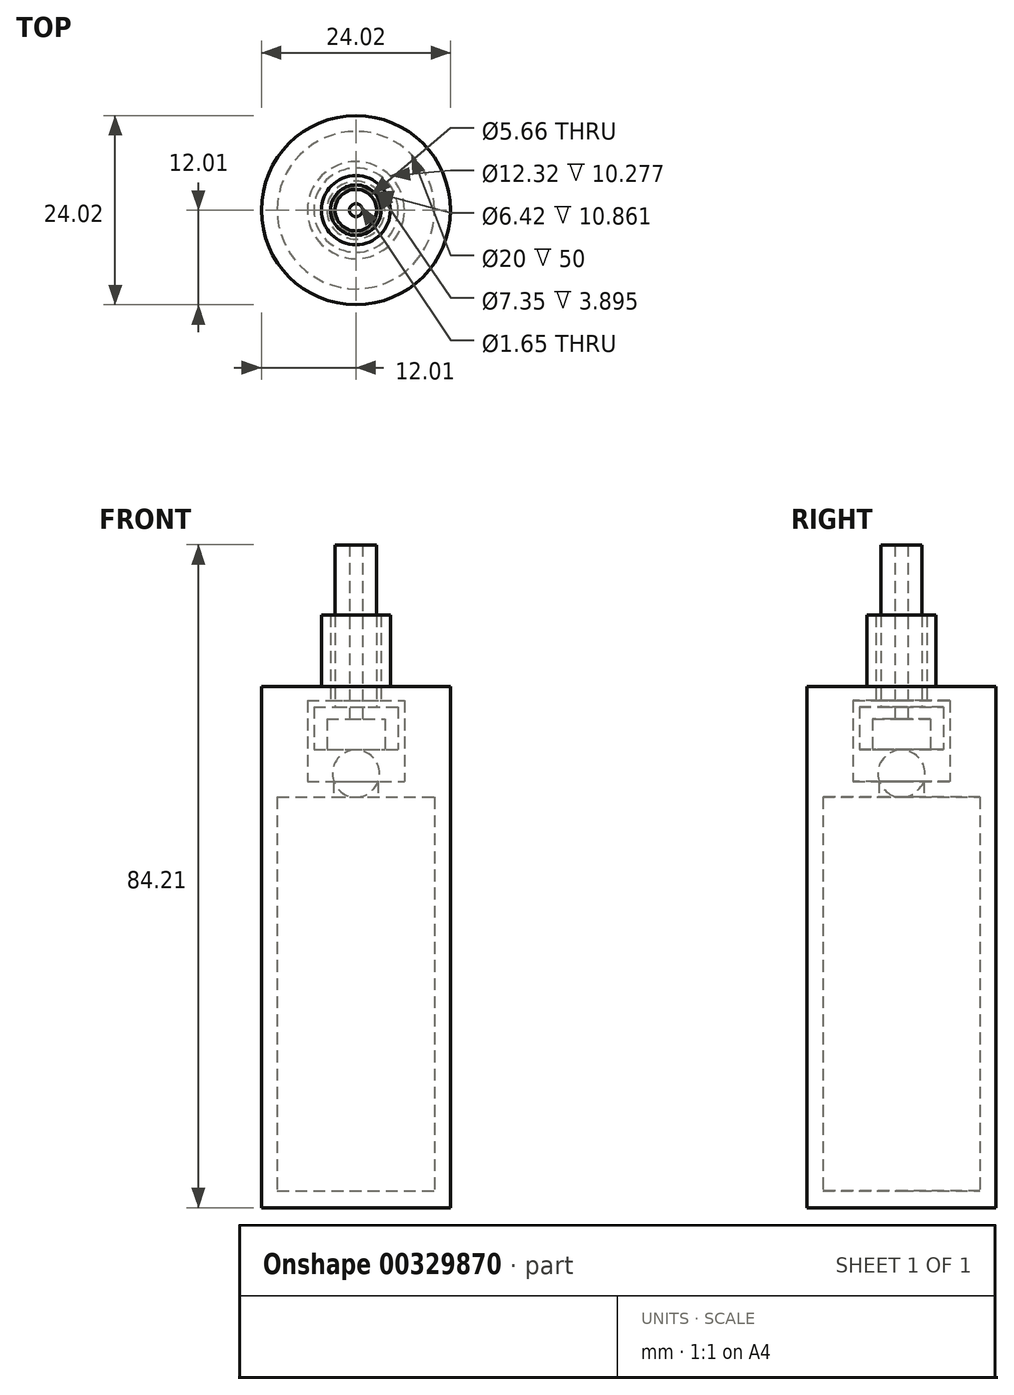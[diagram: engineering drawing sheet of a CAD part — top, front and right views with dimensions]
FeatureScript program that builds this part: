
annotation { "Feature Type Name" : "Feature", "Feature Type Description" : "" }
export const myFeature = defineFeature(function(context is Context, id is Id, definition is map)
    precondition{}
    {
        {
            var Q0;
            Q0=qCreatedBy(makeId("Front.planeOp"),FACE);
            var sketch = newSketch(context, id + "F0", { "sketchPlane" : qUnion([Q0])});
            skLineSegment(sketch, "E0", {"start": v(0, 0) * mm, "end": v(0, 40.48) * mm, "construction": true});
            skLineSegment(sketch, "E1", {"start": v(-10, 50) * mm, "end": v(-10, 0) * mm});
            skLineSegment(sketch, "E2", {"start": v(-10, 0) * mm, "end": v(0, 0) * mm});
            skLineSegment(sketch, "E3", {"start": v(-10, 50) * mm, "end": v(-2.83, 50) * mm});
            skLineSegment(sketch, "E4", {"start": v(-2.83, 50) * mm, "end": v(-2.83, 52) * mm});
            skLineSegment(sketch, "E5", {"start": v(-2.83, 52) * mm, "end": v(-6.16, 52) * mm});
            skLineSegment(sketch, "E6", {"start": v(-6.16, 52) * mm, "end": v(-6.16, 62.28) * mm});
            skArc(sketch, "E7", {"start": v(0, 56) * mm, "mid": v(-3, 53) * mm, "end": v(0, 50) * mm});
            skLineSegment(sketch, "E8", {"start": v(-6.16, 62.28) * mm, "end": v(-3.21, 62.28) * mm});
            skLineSegment(sketch, "E9", {"start": v(-3.21, 62.28) * mm, "end": v(-3.21, 73.14) * mm});
            skLineSegment(sketch, "E10", {"start": v(-3.21, 73.14) * mm, "end": v(-4.38, 73.14) * mm});
            skLineSegment(sketch, "E11", {"start": v(-4.38, 73.14) * mm, "end": v(-4.38, 64.03) * mm});
            skLineSegment(sketch, "E12", {"start": v(-4.38, 64.03) * mm, "end": v(-12, 64.03) * mm});
            skLineSegment(sketch, "E13", {"start": v(-12, 64.03) * mm, "end": v(-12, -2.15) * mm});
            skLineSegment(sketch, "E14", {"start": v(-12, -2.15) * mm, "end": v(0, -2.15) * mm});
            skLineSegment(sketch, "E15", {"start": v(0, -2.15) * mm, "end": v(0, 0) * mm});
            skLineSegment(sketch, "E16", {"start": v(-2.63, 82.06) * mm, "end": v(-2.63, 61.47) * mm});
            skLineSegment(sketch, "E17", {"start": v(-2.63, 61.47) * mm, "end": v(-5.35, 61.47) * mm});
            skLineSegment(sketch, "E18", {"start": v(-5.35, 61.47) * mm, "end": v(-5.35, 56.04) * mm});
            skLineSegment(sketch, "E19", {"start": v(-5.35, 56.04) * mm, "end": v(-3.68, 56.04) * mm});
            skLineSegment(sketch, "E20", {"start": v(-3.68, 56.04) * mm, "end": v(-3.68, 59.94) * mm});
            skLineSegment(sketch, "E21", {"start": v(-3.68, 59.94) * mm, "end": v(-0.83, 59.94) * mm});
            skLineSegment(sketch, "E22", {"start": v(-0.83, 59.94) * mm, "end": v(-0.83, 82.06) * mm});
            skLineSegment(sketch, "E23", {"start": v(-0.83, 82.06) * mm, "end": v(-2.63, 82.06) * mm});
            skLineSegment(sketch, "E24", {"start": v(0, 56) * mm, "end": v(0, 50) * mm});
            skSolve(sketch);
        }
        {
            var Q0;
            Q0 = qSketchRegion(id + "F0", true);
            var Q1;
            Q1=sQuery(id+"F0.wireOp",EDGE,"E0");
            revolve(context, id + "F1", {"surfaceOperationType" : NewSurfaceOperationType.NEW, "entities" : qUnion([Q0]), "axis" : qUnion([Q1]), "revolveType" : RevolveType.FULL});
        }
    });
